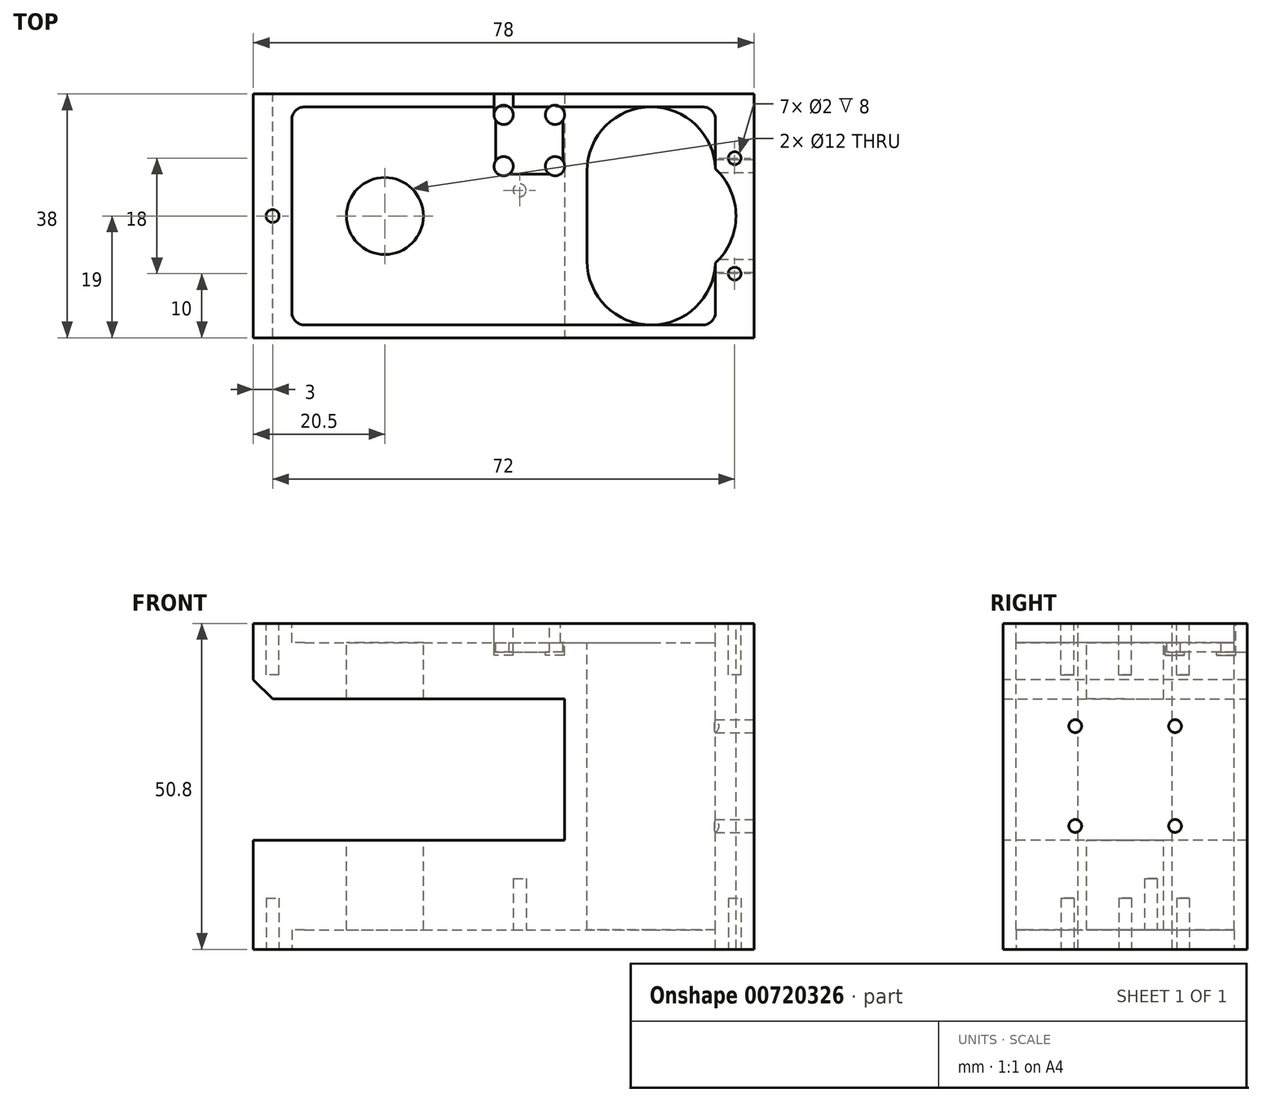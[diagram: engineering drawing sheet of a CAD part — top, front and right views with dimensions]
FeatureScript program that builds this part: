
annotation { "Feature Type Name" : "Feature", "Feature Type Description" : "" }
export const myFeature = defineFeature(function(context is Context, id is Id, definition is map)
    precondition{}
    {
        {
            var Q0;
            Q0=qCreatedBy(makeId("Front.planeOp"),FACE);
            var sketch = newSketch(context, id + "F0", { "sketchPlane" : qUnion([Q0])});
            skLineSegment(sketch, "E0.bottom", {"start": v(0, 0) * mm, "end": v(78, 0) * mm});
            skLineSegment(sketch, "E0.top", {"start": v(0, 50.8) * mm, "end": v(78, 50.8) * mm});
            skLineSegment(sketch, "E0.left", {"start": v(0, 0) * mm, "end": v(0, 50.8) * mm});
            skLineSegment(sketch, "E0.right", {"start": v(78, 0) * mm, "end": v(78, 50.8) * mm});
            skSolve(sketch);
        }
        {
            var Q0;
            Q0 = qSketchRegion(id + "F0", true);
            extrude(context, id + "F1", {"entities" : qUnion([Q0]), "depth" : 38 * mm, "offsetDistance" : 25 * mm});
        }
        {
            var Q0;
            Q0=makeQuery(id+"F1.opExtrude","SWEPT_FACE",FACE,{"disambiguationData":[OSD([sQuery(id+"F0.wireOp",EDGE,"E0.top")])]});
            var sketch = newSketch(context, id + "F2", { "sketchPlane" : qUnion([Q0])});
            skLineSegment(sketch, "E1.bottom", {"start": v(8, -2) * mm, "end": v(70, -2) * mm});
            skLineSegment(sketch, "E1.top", {"start": v(8, -36) * mm, "end": v(70, -36) * mm});
            skLineSegment(sketch, "E1.left", {"start": v(6, -4) * mm, "end": v(6, -34) * mm});
            skLineSegment(sketch, "E1.right", {"start": v(72, -4) * mm, "end": v(72, -34) * mm});
            skPoint(sketch, "E2.visualSharp", {"position": v(6, -2) * mm});
            skArc(sketch, "E2.filletArc", {"start": v(8, -2) * mm, "mid": v(6.59, -2.59) * mm, "end": v(6, -4) * mm});
            skPoint(sketch, "E3.visualSharp", {"position": v(72, -2) * mm});
            skArc(sketch, "E3.filletArc", {"start": v(72, -4) * mm, "mid": v(71.41, -2.59) * mm, "end": v(70, -2) * mm});
            skPoint(sketch, "E4.visualSharp", {"position": v(72, -36) * mm});
            skArc(sketch, "E4.filletArc", {"start": v(70, -36) * mm, "mid": v(71.41, -35.41) * mm, "end": v(72, -34) * mm});
            skPoint(sketch, "E5.visualSharp", {"position": v(6, -36) * mm});
            skArc(sketch, "E5.filletArc", {"start": v(6, -34) * mm, "mid": v(6.59, -35.41) * mm, "end": v(8, -36) * mm});
            skSolve(sketch);
        }
        {
            var Q0;
            Q0=makeQuery(id+"F2.imprint","IMPRINT",FACE,{"disambiguationData":[TD([[makeQuery(id+"F2.imprint","IMPRINT",EDGE,{"derivedFrom":sQuery(id+"F2.wireOp",EDGE,"E1.bottom")}),-1.0]])]});
            extrude(context, id + "F3", {"entities" : qUnion([Q0]), "operationType" : NewBodyOperationType.REMOVE, "oppositeDirection" : true, "depth" : 3 * mm, "offsetDistance" : 25 * mm});
        }
        {
            var Q0;
            Q0=makeQuery(id+"F1.opExtrude","SWEPT_FACE",FACE,{"disambiguationData":[OSD([sQuery(id+"F0.wireOp",EDGE,"E0.top")])]});
            var sketch = newSketch(context, id + "F4", { "sketchPlane" : qUnion([Q0])});
            skLineSegment(sketch, "E6.bottom", {"start": v(62, -2) * mm, "end": v(62, -2) * mm});
            skLineSegment(sketch, "E6.top", {"start": v(62, -36) * mm, "end": v(62, -36) * mm});
            skLineSegment(sketch, "E6.left", {"start": v(52, -12) * mm, "end": v(52, -26) * mm});
            skPoint(sketch, "E7.visualSharp", {"position": v(52, -2) * mm});
            skArc(sketch, "E7.filletArc", {"start": v(62, -2) * mm, "mid": v(54.93, -4.93) * mm, "end": v(52, -12) * mm});
            skPoint(sketch, "E8.visualSharp", {"position": v(52, -36) * mm});
            skArc(sketch, "E8.filletArc", {"start": v(52, -26) * mm, "mid": v(54.93, -33.07) * mm, "end": v(62, -36) * mm});
            skPoint(sketch, "E9.visualSharp", {"position": v(72, -36) * mm});
            skArc(sketch, "E9.filletArc", {"start": v(62, -36) * mm, "mid": v(69.07, -33.07) * mm, "end": v(72, -26) * mm});
            skPoint(sketch, "E10.visualSharp", {"position": v(72, -2) * mm});
            skArc(sketch, "E10.filletArc", {"start": v(72, -12) * mm, "mid": v(69.07, -4.93) * mm, "end": v(62, -2) * mm});
            skArc(sketch, "E11", {"start": v(72, -26.34) * mm, "mid": v(75.2, -19) * mm, "end": v(72, -11.66) * mm});
            skSolve(sketch);
        }
        {
            var Q0;
            Q0 = qSketchRegion(id + "F4", true);
            var Q1;
            Q1=makeQuery(id+"F1.opExtrude","SWEPT_FACE",FACE,{"disambiguationData":[OSD([sQuery(id+"F0.wireOp",EDGE,"E0.bottom")])]});
            extrude(context, id + "F5", {"entities" : qUnion([Q0]), "operationType" : NewBodyOperationType.REMOVE, "endBound" : BoundingType.UP_TO_SURFACE, "oppositeDirection" : true, "depth" : 25 * mm, "endBoundEntityFace" : qUnion([Q1]), "offsetDistance" : 25 * mm});
        }
        {
            var Q0;
            Q0=makeQuery(id+"F1.opExtrude","SWEPT_FACE",FACE,{"disambiguationData":[OSD([sQuery(id+"F0.wireOp",EDGE,"E0.top")])]});
            var sketch = newSketch(context, id + "F6", { "sketchPlane" : qUnion([Q0])});
            skLineSegment(sketch, "E12.bottom", {"start": v(38.75, -2) * mm, "end": v(47.25, -2) * mm});
            skLineSegment(sketch, "E12.top", {"start": v(38.75, -12.5) * mm, "end": v(47.25, -12.5) * mm});
            skLineSegment(sketch, "E12.left", {"start": v(37.75, -3) * mm, "end": v(37.75, -11.5) * mm});
            skLineSegment(sketch, "E12.right", {"start": v(48.25, -3) * mm, "end": v(48.25, -11.5) * mm});
            skPoint(sketch, "E13.visualSharp", {"position": v(37.75, -2) * mm});
            skArc(sketch, "E13.filletArc", {"start": v(38.75, -2) * mm, "mid": v(38.04, -2.3) * mm, "end": v(37.75, -3) * mm});
            skPoint(sketch, "E14.visualSharp", {"position": v(37.75, -12.5) * mm});
            skArc(sketch, "E14.filletArc", {"start": v(37.75, -11.5) * mm, "mid": v(38.04, -12.2) * mm, "end": v(38.75, -12.5) * mm});
            skPoint(sketch, "E15.visualSharp", {"position": v(48.25, -12.5) * mm});
            skArc(sketch, "E15.filletArc", {"start": v(47.25, -12.5) * mm, "mid": v(47.96, -12.2) * mm, "end": v(48.25, -11.5) * mm});
            skPoint(sketch, "E16.visualSharp", {"position": v(48.25, -2) * mm});
            skArc(sketch, "E16.filletArc", {"start": v(48.25, -3) * mm, "mid": v(47.96, -2.3) * mm, "end": v(47.25, -2) * mm});
            skSolve(sketch);
        }
        {
            var Q0;
            Q0=makeQuery(id+"F6.imprint","IMPRINT",FACE,{"disambiguationData":[TD([[makeQuery(id+"F6.imprint","IMPRINT",EDGE,{"derivedFrom":sQuery(id+"F6.wireOp",EDGE,"E12.bottom")}),-1.0]])]});
            extrude(context, id + "F7", {"entities" : qUnion([Q0]), "operationType" : NewBodyOperationType.REMOVE, "oppositeDirection" : true, "depth" : 4.5 * mm, "offsetDistance" : 25 * mm});
        }
        {
            var Q0;
            Q0=makeQuery(id+"F1.opExtrude","SWEPT_FACE",FACE,{"disambiguationData":[OSD([sQuery(id+"F0.wireOp",EDGE,"E0.top")])]});
            var sketch = newSketch(context, id + "F8", { "sketchPlane" : qUnion([Q0])});
            skCircle(sketch, "E17", {"center": v(47, -11.25) * mm, "radius": 1.5 * mm});
            skCircle(sketch, "E18", {"center": v(39, -11.25) * mm, "radius": 1.5 * mm});
            skCircle(sketch, "E19", {"center": v(39, -3.25) * mm, "radius": 1.5 * mm});
            skCircle(sketch, "E20", {"center": v(47, -3.25) * mm, "radius": 1.5 * mm});
            skSolve(sketch);
        }
        {
            var Q0;
            Q0 = qSketchRegion(id + "F8", true);
            extrude(context, id + "F9", {"entities" : qUnion([Q0]), "operationType" : NewBodyOperationType.REMOVE, "oppositeDirection" : true, "depth" : 5 * mm, "offsetDistance" : 25 * mm});
        }
        {
            var Q0;
            Q0=makeQuery(id+"F1.opExtrude","SWEPT_FACE",FACE,{"disambiguationData":[OSD([sQuery(id+"F0.wireOp",EDGE,"E0.top")])]});
            var sketch = newSketch(context, id + "F10", { "sketchPlane" : qUnion([Q0])});
            skLineSegment(sketch, "E21.bottom", {"start": v(37.5, -3.25) * mm, "end": v(40.5, -3.25) * mm});
            skLineSegment(sketch, "E21.top", {"start": v(37.5, 0) * mm, "end": v(40.5, 0) * mm});
            skLineSegment(sketch, "E21.left", {"start": v(37.5, -3.25) * mm, "end": v(37.5, 0) * mm});
            skLineSegment(sketch, "E21.right", {"start": v(40.5, -3.25) * mm, "end": v(40.5, 0) * mm});
            skSolve(sketch);
        }
        {
            var Q0;
            Q0 = qSketchRegion(id + "F10", true);
            extrude(context, id + "F11", {"entities" : qUnion([Q0]), "operationType" : NewBodyOperationType.REMOVE, "oppositeDirection" : true, "depth" : 4.5 * mm, "offsetDistance" : 25 * mm});
        }
        {
            var Q0;
            Q0=makeQuery(id+"F1.opExtrude","SWEPT_FACE",FACE,{"disambiguationData":[OSD([sQuery(id+"F0.wireOp",EDGE,"E0.top")])]});
            var sketch = newSketch(context, id + "F12", { "sketchPlane" : qUnion([Q0])});
            skCircle(sketch, "E22", {"center": v(20.5, -19) * mm, "radius": 6 * mm});
            skSolve(sketch);
        }
        {
            var Q0;
            Q0 = qSketchRegion(id + "F12", true);
            extrude(context, id + "F13", {"entities" : qUnion([Q0]), "operationType" : NewBodyOperationType.REMOVE, "oppositeDirection" : true, "depth" : 51 * mm, "offsetDistance" : 25 * mm});
        }
        {
            var Q0;
            Q0=makeQuery(id+"F1.opExtrude","SWEPT_FACE",FACE,{"disambiguationData":[OSD([sQuery(id+"F0.wireOp",EDGE,"E0.bottom")])]});
            var sketch = newSketch(context, id + "F14", { "sketchPlane" : qUnion([Q0])});
            skLineSegment(sketch, "E23.bottom", {"start": v(8, 36) * mm, "end": v(70, 36) * mm});
            skLineSegment(sketch, "E23.top", {"start": v(8, 2) * mm, "end": v(70, 2) * mm});
            skLineSegment(sketch, "E23.left", {"start": v(6, 34) * mm, "end": v(6, 4) * mm});
            skLineSegment(sketch, "E23.right", {"start": v(72, 34) * mm, "end": v(72, 4) * mm});
            skPoint(sketch, "E24.visualSharp", {"position": v(6, 36) * mm});
            skArc(sketch, "E24.filletArc", {"start": v(8, 36) * mm, "mid": v(6.59, 35.41) * mm, "end": v(6, 34) * mm});
            skPoint(sketch, "E25.visualSharp", {"position": v(6, 2) * mm});
            skArc(sketch, "E25.filletArc", {"start": v(6, 4) * mm, "mid": v(6.59, 2.59) * mm, "end": v(8, 2) * mm});
            skPoint(sketch, "E26.visualSharp", {"position": v(72, 36) * mm});
            skArc(sketch, "E26.filletArc", {"start": v(72, 34) * mm, "mid": v(71.41, 35.41) * mm, "end": v(70, 36) * mm});
            skPoint(sketch, "E27.visualSharp", {"position": v(72, 2) * mm});
            skArc(sketch, "E27.filletArc", {"start": v(70, 2) * mm, "mid": v(71.41, 2.59) * mm, "end": v(72, 4) * mm});
            skSolve(sketch);
        }
        {
            var Q0;
            Q0 = qSketchRegion(id + "F14", true);
            extrude(context, id + "F15", {"entities" : qUnion([Q0]), "operationType" : NewBodyOperationType.REMOVE, "oppositeDirection" : true, "depth" : 3 * mm, "offsetDistance" : 25 * mm});
        }
        {
            var Q0;
            Q0=makeQuery(id+"F1.opExtrude","CAP_FACE",FACE,{"disambiguationData":[OSD([sQuery(id+"F0.wireOp",EDGE,"E0.bottom"),sQuery(id+"F0.wireOp",EDGE,"E0.top"),sQuery(id+"F0.wireOp",EDGE,"E0.left"),sQuery(id+"F0.wireOp",EDGE,"E0.right")])],"isStart":false});
            var sketch = newSketch(context, id + "F16", { "sketchPlane" : qUnion([Q0])});
            skLineSegment(sketch, "E28.bottom", {"start": v(0, 39) * mm, "end": v(48.5, 39) * mm});
            skLineSegment(sketch, "E28.top", {"start": v(0, 17) * mm, "end": v(48.5, 17) * mm});
            skLineSegment(sketch, "E28.left", {"start": v(0, 39) * mm, "end": v(0, 17) * mm});
            skLineSegment(sketch, "E28.right", {"start": v(48.5, 39) * mm, "end": v(48.5, 17) * mm});
            skSolve(sketch);
        }
        {
            var Q0;
            Q0 = qSketchRegion(id + "F16", true);
            var Q1;
            Q1=makeQuery(id+"F1.opExtrude","CAP_FACE",FACE,{"disambiguationData":[OSD([sQuery(id+"F0.wireOp",EDGE,"E0.bottom"),sQuery(id+"F0.wireOp",EDGE,"E0.top"),sQuery(id+"F0.wireOp",EDGE,"E0.left"),sQuery(id+"F0.wireOp",EDGE,"E0.right")])],"isStart":true});
            extrude(context, id + "F17", {"entities" : qUnion([Q0]), "operationType" : NewBodyOperationType.REMOVE, "endBound" : BoundingType.UP_TO_SURFACE, "oppositeDirection" : true, "depth" : 25 * mm, "endBoundEntityFace" : qUnion([Q1]), "offsetDistance" : 25 * mm});
        }
        {
            var Q0;
            Q0=makeQuery(id+"F17.boolean.opBoolean","COPY",EDGE,{"derivedFrom":makeQuery(id+"F17.opExtrude","SWEPT_EDGE",EDGE,{"disambiguationData":[OSD([sQuery(id+"F0.wireOp",EDGE,"E0.left"),sQuery(id+"F16.wireOp",EDGE,"E28.bottom"),sQuery(id+"F16.wireOp",EDGE,"E28.left")])]})});
            var Q1;
            Q1=makeQuery(id+"F17.boolean.opBoolean","COPY",EDGE,{"derivedFrom":makeQuery(id+"F17.opExtrude","SWEPT_EDGE",EDGE,{"disambiguationData":[OSD([sQuery(id+"F0.wireOp",EDGE,"E0.left"),sQuery(id+"F16.wireOp",EDGE,"E28.top"),sQuery(id+"F16.wireOp",EDGE,"E28.left")])]})});
            chamfer(context, id + "F18", {"entities" : qUnion([Q0, Q1]), "width" : 3 * mm, "tangentPropagation" : true});
        }
        {
            var Q0;
            Q0=makeQuery(id+"F1.opExtrude","SWEPT_FACE",FACE,{"disambiguationData":[OSD([sQuery(id+"F0.wireOp",EDGE,"E0.top")])]});
            var sketch = newSketch(context, id + "F19", { "sketchPlane" : qUnion([Q0])});
            skCircle(sketch, "E29", {"center": v(3, -19) * mm, "radius": 1 * mm});
            skCircle(sketch, "E30", {"center": v(75, -10) * mm, "radius": 1 * mm});
            skCircle(sketch, "E31", {"center": v(75, -28) * mm, "radius": 1 * mm});
            skSolve(sketch);
        }
        {
            var Q0;
            Q0 = qSketchRegion(id + "F19", true);
            extrude(context, id + "F20", {"entities" : qUnion([Q0]), "operationType" : NewBodyOperationType.REMOVE, "oppositeDirection" : true, "depth" : 8 * mm, "offsetDistance" : 25 * mm});
        }
        {
            var Q0;
            Q0=makeQuery(id+"F1.opExtrude","SWEPT_FACE",FACE,{"disambiguationData":[OSD([sQuery(id+"F0.wireOp",EDGE,"E0.bottom")])]});
            var sketch = newSketch(context, id + "F21", { "sketchPlane" : qUnion([Q0])});
            skCircle(sketch, "E32", {"center": v(75, 28) * mm, "radius": 1 * mm});
            skCircle(sketch, "E33", {"center": v(75, 10) * mm, "radius": 1 * mm});
            skCircle(sketch, "E34", {"center": v(3, 19) * mm, "radius": 1 * mm});
            skSolve(sketch);
        }
        {
            var Q0;
            Q0 = qSketchRegion(id + "F21", true);
            extrude(context, id + "F22", {"entities" : qUnion([Q0]), "operationType" : NewBodyOperationType.REMOVE, "oppositeDirection" : true, "depth" : 8 * mm, "offsetDistance" : 25 * mm});
        }
        {
            var Q0;
            {var subQ0=sQuery(id+"F14.wireOp",EDGE,"E23.top");var subQ1=sQuery(id+"F14.wireOp",EDGE,"E25.filletArc");var subQ2=sQuery(id+"F14.wireOp",EDGE,"E24.filletArc");var subQ3=sQuery(id+"F14.wireOp",EDGE,"E23.left");var subQ4=sQuery(id+"F14.wireOp",EDGE,"E23.bottom");var subQ5=makeQuery(id+"F15.opExtrude","CAP_FACE",FACE,{"disambiguationData":[OSD([subQ4,subQ0,subQ3,sQuery(id+"F14.wireOp",EDGE,"E23.right"),subQ2,subQ1,sQuery(id+"F14.wireOp",EDGE,"E26.filletArc"),sQuery(id+"F14.wireOp",EDGE,"E27.filletArc")])],"isStart":false});Q0=makeQuery(id+"F15.boolean.opBoolean","COPY",FACE,{"disambiguationData":[TD([makeQuery(id+"F5.boolean.opBoolean","COPY",FACE,{"derivedFrom":makeQuery(id+"F5.opExtrude","SWEPT_FACE",FACE,{"disambiguationData":[OSD([sQuery(id+"F4.wireOp",EDGE,"E6.left")])]})})])],"derivedFrom":subQ5});}
            var sketch = newSketch(context, id + "F23", { "sketchPlane" : qUnion([Q0])});
            skCircle(sketch, "E35", {"center": v(41.5, 15) * mm, "radius": 1 * mm});
            skSolve(sketch);
        }
        {
            var Q0;
            Q0 = qSketchRegion(id + "F23", true);
            extrude(context, id + "F24", {"entities" : qUnion([Q0]), "operationType" : NewBodyOperationType.REMOVE, "oppositeDirection" : true, "depth" : 8 * mm, "offsetDistance" : 25 * mm});
        }
        {
            var Q0;
            Q0=makeQuery(id+"F1.opExtrude","SWEPT_FACE",FACE,{"disambiguationData":[OSD([sQuery(id+"F0.wireOp",EDGE,"E0.right")])]});
            var sketch = newSketch(context, id + "F25", { "sketchPlane" : qUnion([Q0])});
            skCircle(sketch, "E36", {"center": v(-19, 27) * mm, "radius": 11 * mm, "construction": true});
            skCircle(sketch, "E37", {"center": v(-26.78, 34.78) * mm, "radius": 1 * mm});
            skCircle(sketch, "E38", {"center": v(-11.22, 34.78) * mm, "radius": 1 * mm});
            skCircle(sketch, "E39", {"center": v(-26.78, 19.22) * mm, "radius": 1 * mm});
            skCircle(sketch, "E40", {"center": v(-11.22, 19.22) * mm, "radius": 1 * mm});
            skLineSegment(sketch, "E41", {"start": v(-30, 27) * mm, "end": v(-8, 27) * mm, "construction": true});
            skLineSegment(sketch, "E42", {"start": v(-19, 27) * mm, "end": v(-11.22, 34.78) * mm, "construction": true});
            skLineSegment(sketch, "E43", {"start": v(-19, 27) * mm, "end": v(-26.78, 19.22) * mm, "construction": true});
            skLineSegment(sketch, "E44", {"start": v(-26.78, 34.78) * mm, "end": v(-19, 27) * mm, "construction": true});
            skLineSegment(sketch, "E45", {"start": v(-19, 27) * mm, "end": v(-11.22, 19.22) * mm, "construction": true});
            skSolve(sketch);
        }
        {
            var Q0;
            Q0 = qSketchRegion(id + "F25", true);
            extrude(context, id + "F26", {"entities" : qUnion([Q0]), "operationType" : NewBodyOperationType.REMOVE, "oppositeDirection" : true, "depth" : 10 * mm, "offsetDistance" : 25 * mm});
        }
    });
